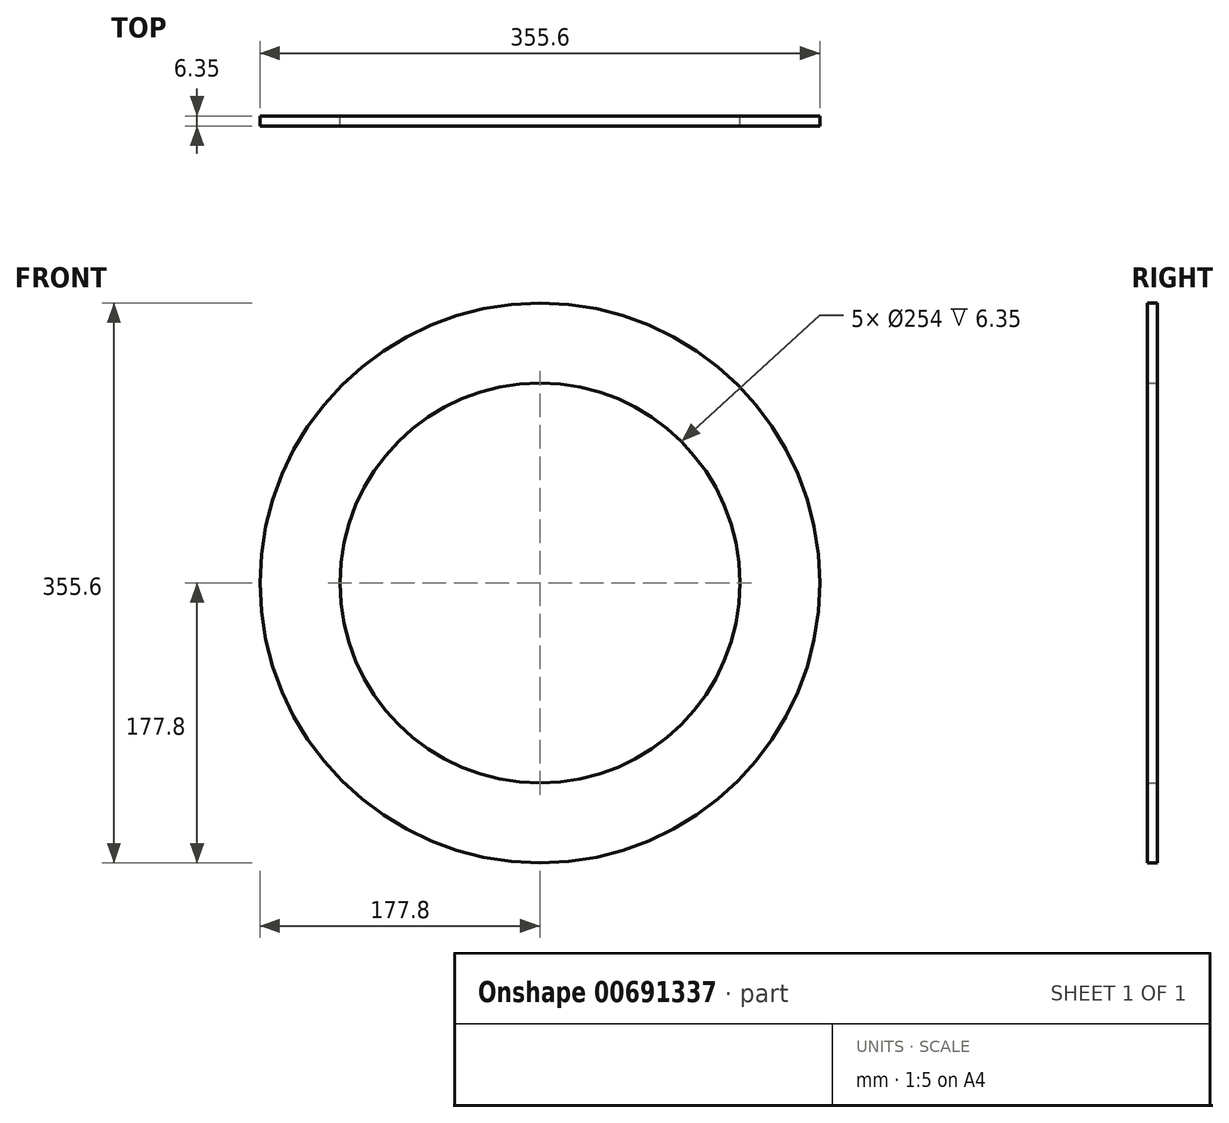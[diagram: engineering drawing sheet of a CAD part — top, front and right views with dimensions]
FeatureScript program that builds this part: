
annotation { "Feature Type Name" : "Feature", "Feature Type Description" : "" }
export const myFeature = defineFeature(function(context is Context, id is Id, definition is map)
    precondition{}
    {
        {
            var Q0;
            Q0=qCreatedBy(makeId("Front.planeOp"),FACE);
            var sketch = newSketch(context, id + "F0", { "sketchPlane" : qUnion([Q0])});
            skCircle(sketch, "E0", {"center": v(0, 0) * mm, "radius": 127 * mm});
            skCircle(sketch, "E1.0", {"center": v(0, 0) * mm, "radius": 177.8 * mm});
            skSolve(sketch);
        }
        {
            var Q0;
            Q0=makeQuery(id+"F0.imprint","IMPRINT",FACE,{"disambiguationData":[TD([[makeQuery(id+"F0.imprint","IMPRINT",EDGE,{"derivedFrom":sQuery(id+"F0.wireOp",EDGE,"E0")}),-1.0]])]});
            extrude(context, id + "F1", {"entities" : qUnion([Q0]), "depth" : 6.35 * mm, "offsetDistance" : 25.4 * mm});
        }
    });
